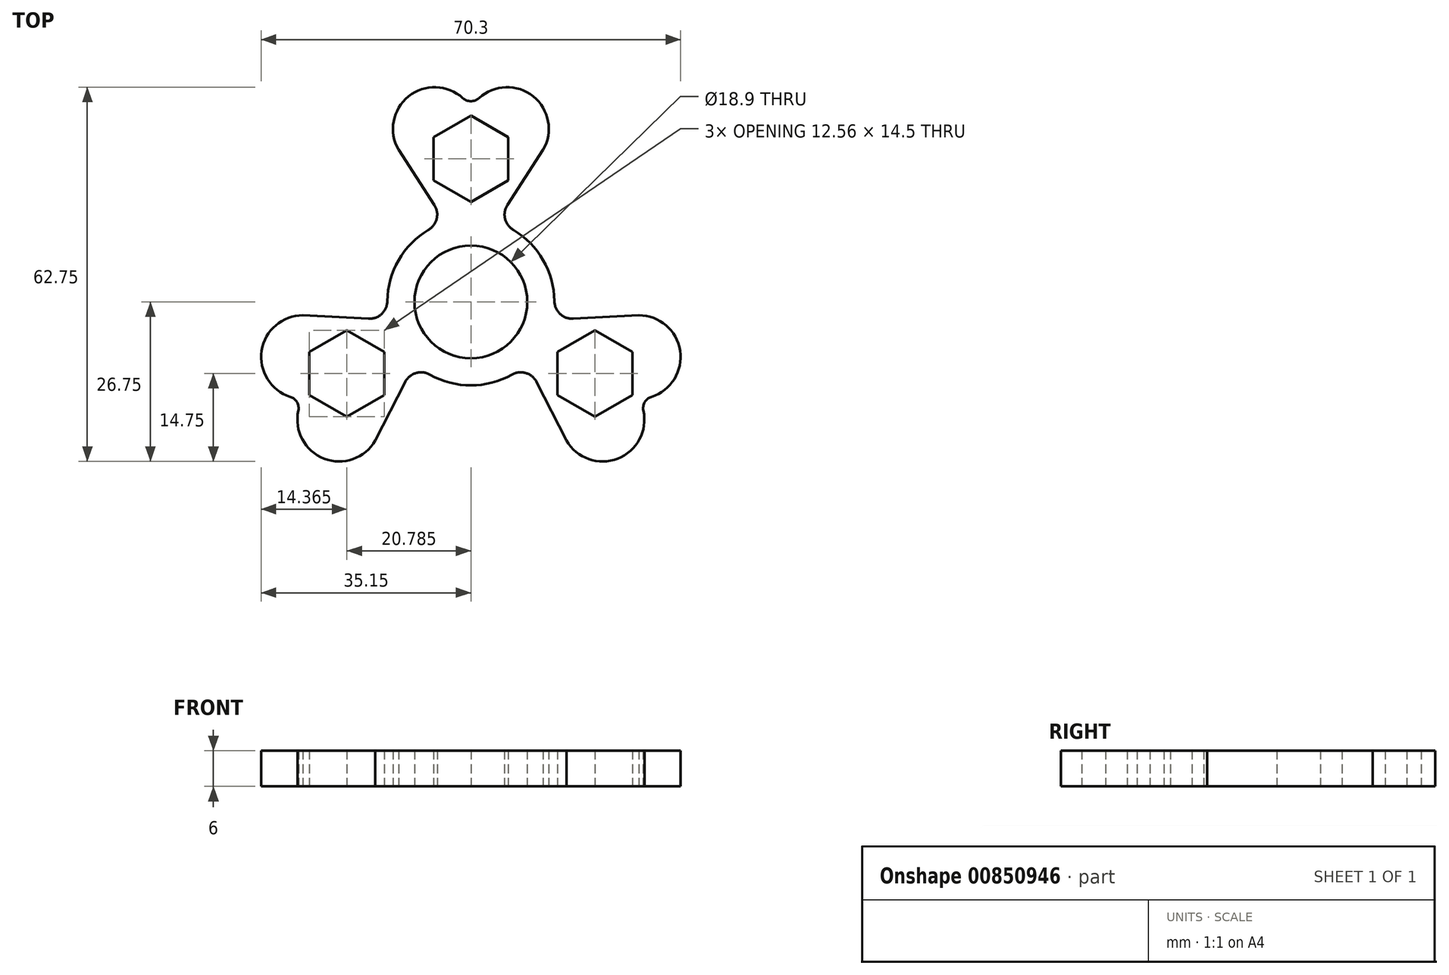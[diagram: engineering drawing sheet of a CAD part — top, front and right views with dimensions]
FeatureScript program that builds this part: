
annotation { "Feature Type Name" : "Feature", "Feature Type Description" : "" }
export const myFeature = defineFeature(function(context is Context, id is Id, definition is map)
    precondition{}
    {
        {
            var Q0;
            Q0=qCreatedBy(makeId("Top.planeOp"),FACE);
            var sketch = newSketch(context, id + "F0", { "sketchPlane" : qUnion([Q0])});
            skCircle(sketch, "E0", {"center": v(0, 0) * mm, "radius": 9.45 * mm});
            skCircle(sketch, "E1", {"center": v(0, 0) * mm, "radius": 14 * mm});
            skSolve(sketch);
        }
        {
            var Q0;
            Q0=makeQuery(id+"F0.imprint","IMPRINT",FACE,{"disambiguationData":[TD([[makeQuery(id+"F0.imprint","IMPRINT",EDGE,{"derivedFrom":sQuery(id+"F0.wireOp",EDGE,"E0")}),-1.0]])]});
            extrude(context, id + "F1", {"entities" : qUnion([Q0]), "depth" : 6 * mm, "offsetDistance" : 25 * mm});
        }
        {
            var Q0;
            Q0=qCreatedBy(makeId("Top.planeOp"),FACE);
            var sketch = newSketch(context, id + "F2", { "sketchPlane" : qUnion([Q0])});
            skLineSegment(sketch, "E2", {"start": v(6.13, 16.27) * mm, "end": v(12.12, 25.5) * mm});
            skArc(sketch, "E3", {"start": v(12.12, 25.5) * mm, "mid": v(10.45, 34.45) * mm, "end": v(1.35, 34.17) * mm});
            skLineSegment(sketch, "E4.trimOffspring", {"start": v(0, 32.5) * mm, "end": v(0, 67.1) * mm, "construction": true});
            skLineSegment(sketch, "E5.trimOffspring", {"start": v(0, 19) * mm, "end": v(0, 41) * mm, "construction": true});
            skArc(sketch, "E6.MirrorCS", {"start": v(-12.12, 25.5) * mm, "mid": v(-10.45, 34.45) * mm, "end": v(-1.35, 34.17) * mm});
            skPoint(sketch, "E7.visualSharp", {"position": v(0, 32.5) * mm});
            skArc(sketch, "E7.filletArc", {"start": v(-1.35, 34.17) * mm, "mid": v(0, 33.65) * mm, "end": v(1.35, 34.17) * mm});
            skPoint(sketch, "E8.0.midPoint", {"position": v(0, 30) * mm});
            skCircle(sketch, "E9.0", {"center": v(0, 0) * mm, "radius": 14 * mm});
            skArc(sketch, "E10", {"start": v(6.13, 16.27) * mm, "mid": v(5.73, 13.95) * mm, "end": v(7.12, 12.05) * mm});
            skPoint(sketch, "E11.orphan", {"position": v(1.19, 8.66) * mm});
            skPoint(sketch, "E12.orphan", {"position": v(-1.19, 8.66) * mm});
            skArc(sketch, "E13.MirrorCS", {"start": v(-6.13, 16.27) * mm, "mid": v(-5.73, 13.95) * mm, "end": v(-7.12, 12.05) * mm});
            skLineSegment(sketch, "E14", {"start": v(-6.13, 16.27) * mm, "end": v(-12.12, 25.5) * mm});
            skPoint(sketch, "E15.1.1", {"position": v(-28.15, -16.25) * mm});
            skPoint(sketch, "E15.1.2", {"position": v(-25.98, -15) * mm});
            skPoint(sketch, "E15.1.3", {"position": v(-8.1, -3.3) * mm});
            skArc(sketch, "E15.1.4", {"start": v(-28.15, -2.25) * mm, "mid": v(-35.06, -8.18) * mm, "end": v(-30.27, -15.92) * mm});
            skArc(sketch, "E15.1.6", {"start": v(-17.16, -2.83) * mm, "mid": v(-14.94, -2.02) * mm, "end": v(-14, 0.14) * mm});
            skLineSegment(sketch, "E15.1.7", {"start": v(-11.03, -13.44) * mm, "end": v(-16.02, -23.25) * mm});
            skLineSegment(sketch, "E15.1.8", {"start": v(-16.45, -9.5) * mm, "end": v(-35.5, -20.5) * mm, "construction": true});
            skArc(sketch, "E15.1.11", {"start": v(-16.02, -23.25) * mm, "mid": v(-24.61, -26.28) * mm, "end": v(-28.92, -18.25) * mm});
            skLineSegment(sketch, "E15.1.12", {"start": v(-17.16, -2.83) * mm, "end": v(-28.15, -2.25) * mm});
            skPoint(sketch, "E15.1.14", {"position": v(-6.9, -5.36) * mm});
            skArc(sketch, "E15.1.16", {"start": v(-11.03, -13.44) * mm, "mid": v(-9.22, -11.93) * mm, "end": v(-6.88, -12.2) * mm});
            skArc(sketch, "E15.1.17", {"start": v(-28.92, -18.25) * mm, "mid": v(-29.14, -16.83) * mm, "end": v(-30.27, -15.92) * mm});
            skPoint(sketch, "E15.2.1", {"position": v(28.15, -16.25) * mm});
            skPoint(sketch, "E15.2.2", {"position": v(25.98, -15) * mm});
            skPoint(sketch, "E15.2.3", {"position": v(6.9, -5.36) * mm});
            skArc(sketch, "E15.2.4", {"start": v(16.02, -23.25) * mm, "mid": v(24.61, -26.28) * mm, "end": v(28.92, -18.25) * mm});
            skArc(sketch, "E15.2.6", {"start": v(11.03, -13.44) * mm, "mid": v(9.22, -11.93) * mm, "end": v(6.88, -12.2) * mm});
            skLineSegment(sketch, "E15.2.7", {"start": v(17.16, -2.83) * mm, "end": v(28.15, -2.25) * mm});
            skLineSegment(sketch, "E15.2.8", {"start": v(16.45, -9.5) * mm, "end": v(35.5, -20.5) * mm, "construction": true});
            skArc(sketch, "E15.2.11", {"start": v(28.15, -2.25) * mm, "mid": v(35.06, -8.18) * mm, "end": v(30.27, -15.92) * mm});
            skLineSegment(sketch, "E15.2.12", {"start": v(11.03, -13.44) * mm, "end": v(16.02, -23.25) * mm});
            skPoint(sketch, "E15.2.14", {"position": v(8.1, -3.3) * mm});
            skArc(sketch, "E15.2.16", {"start": v(17.16, -2.83) * mm, "mid": v(14.94, -2.02) * mm, "end": v(14, 0.14) * mm});
            skArc(sketch, "E15.2.17", {"start": v(30.27, -15.92) * mm, "mid": v(29.14, -16.83) * mm, "end": v(28.92, -18.25) * mm});
            skCircle(sketch, "E16.cCircle", {"center": v(0, 24) * mm, "radius": 7.25 * mm, "construction": true});
            skLineSegment(sketch, "E16.0", {"start": v(0, 31.25) * mm, "end": v(6.28, 27.62) * mm});
            skLineSegment(sketch, "E16.1", {"start": v(6.28, 27.62) * mm, "end": v(6.28, 20.38) * mm});
            skLineSegment(sketch, "E16.2", {"start": v(6.28, 20.38) * mm, "end": v(0, 16.75) * mm});
            skLineSegment(sketch, "E16.3", {"start": v(0, 16.75) * mm, "end": v(-6.28, 20.38) * mm});
            skLineSegment(sketch, "E16.4", {"start": v(-6.28, 20.37) * mm, "end": v(-6.28, 27.63) * mm});
            skLineSegment(sketch, "E16.5", {"start": v(-6.28, 27.63) * mm, "end": v(0, 31.25) * mm});
            skLineSegment(sketch, "E17.1.0", {"start": v(-27.06, -8.37) * mm, "end": v(-20.78, -4.75) * mm});
            skLineSegment(sketch, "E17.1.1", {"start": v(-27.06, -15.62) * mm, "end": v(-27.06, -8.37) * mm});
            skLineSegment(sketch, "E17.1.2", {"start": v(-20.78, -19.25) * mm, "end": v(-27.06, -15.62) * mm});
            skLineSegment(sketch, "E17.1.3", {"start": v(-14.5, -15.62) * mm, "end": v(-20.78, -19.25) * mm});
            skLineSegment(sketch, "E17.1.4", {"start": v(-14.5, -8.37) * mm, "end": v(-14.5, -15.62) * mm});
            skLineSegment(sketch, "E17.1.5", {"start": v(-20.78, -4.75) * mm, "end": v(-14.5, -8.38) * mm});
            skLineSegment(sketch, "E17.2.0", {"start": v(20.78, -19.25) * mm, "end": v(14.5, -15.63) * mm});
            skLineSegment(sketch, "E17.2.1", {"start": v(27.06, -15.63) * mm, "end": v(20.78, -19.25) * mm});
            skLineSegment(sketch, "E17.2.2", {"start": v(27.06, -8.38) * mm, "end": v(27.06, -15.62) * mm});
            skLineSegment(sketch, "E17.2.3", {"start": v(20.78, -4.75) * mm, "end": v(27.06, -8.37) * mm});
            skLineSegment(sketch, "E17.2.4", {"start": v(14.5, -8.38) * mm, "end": v(20.78, -4.75) * mm});
            skLineSegment(sketch, "E17.2.5", {"start": v(14.5, -15.63) * mm, "end": v(14.5, -8.37) * mm});
            skSolve(sketch);
        }
        {
            var Q0;
            Q0=makeQuery(id+"F2.imprint","IMPRINT",FACE,{"disambiguationData":[TD([[makeQuery(id+"F2.imprint","IMPRINT",EDGE,{"derivedFrom":sQuery(id+"F2.wireOp",EDGE,"E2")}),1.0]])]});
            var Q1;
            Q1=makeQuery(id+"F2.imprint","IMPRINT",FACE,{"disambiguationData":[TD([[makeQuery(id+"F2.imprint","IMPRINT",EDGE,{"derivedFrom":sQuery(id+"F2.wireOp",EDGE,"E15.1.0")}),1.0]])]});
            var Q2;
            Q2=makeQuery(id+"F2.imprint","IMPRINT",FACE,{"disambiguationData":[TD([[makeQuery(id+"F2.imprint","IMPRINT",EDGE,{"derivedFrom":sQuery(id+"F2.wireOp",EDGE,"E15.2.0")}),1.0]])]});
            var Q3;
            Q3=makeQuery(id+"F2.imprint","IMPRINT",FACE,{"disambiguationData":[TD([[makeQuery(id+"F2.imprint","IMPRINT",EDGE,{"derivedFrom":sQuery(id+"F2.wireOp",EDGE,"E15.2.4")}),1.0]])]});
            var Q4;
            Q4=makeQuery(id+"F2.imprint","IMPRINT",FACE,{"disambiguationData":[TD([[makeQuery(id+"F2.imprint","IMPRINT",EDGE,{"derivedFrom":sQuery(id+"F2.wireOp",EDGE,"E15.1.4")}),1.0]])]});
            extrude(context, id + "F3", {"entities" : qUnion([Q0, Q1, Q2, Q3, Q4]), "operationType" : NewBodyOperationType.ADD, "depth" : 6 * mm, "offsetDistance" : 25 * mm});
        }
    });
